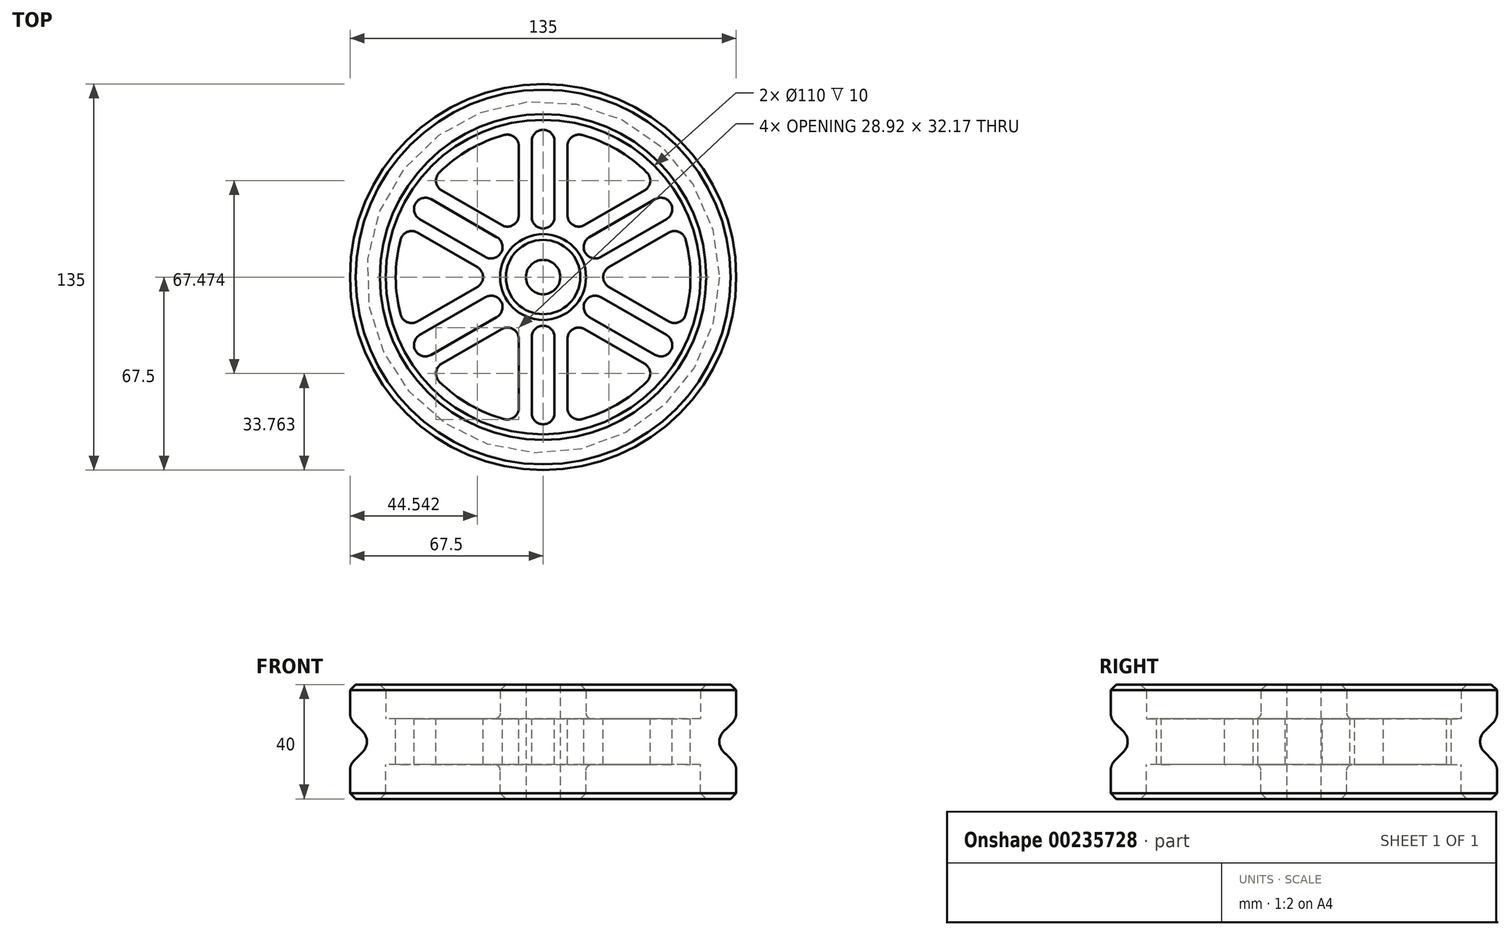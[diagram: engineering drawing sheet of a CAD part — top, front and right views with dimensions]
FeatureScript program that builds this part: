
annotation { "Feature Type Name" : "Feature", "Feature Type Description" : "" }
export const myFeature = defineFeature(function(context is Context, id is Id, definition is map)
    precondition{}
    {
        {
            var Q0;
            Q0=qCreatedBy(makeId("Top.planeOp"),FACE);
            var sketch = newSketch(context, id + "F0", { "sketchPlane" : qUnion([Q0])});
            skCircle(sketch, "E0", {"center": v(0, 0) * mm, "radius": 67.5 * mm});
            skCircle(sketch, "E1", {"center": v(0, 0) * mm, "radius": 55 * mm});
            skCircle(sketch, "E2", {"center": v(0, 0) * mm, "radius": 51.5 * mm});
            skCircle(sketch, "E3", {"center": v(0, 0) * mm, "radius": 47.5 * mm, "construction": true});
            skCircle(sketch, "E4", {"center": v(0, 0) * mm, "radius": 21 * mm, "construction": true});
            skCircle(sketch, "E5", {"center": v(0, 0) * mm, "radius": 6 * mm});
            skCircle(sketch, "E6", {"center": v(0, 0) * mm, "radius": 15 * mm});
            skCircle(sketch, "E7", {"center": v(0, 0) * mm, "radius": 17 * mm, "construction": true});
            skLineSegment(sketch, "E8", {"start": v(0, 0) * mm, "end": v(0, 51.5) * mm, "construction": true});
            skCircle(sketch, "E9", {"center": v(0, 21) * mm, "radius": 4 * mm});
            skCircle(sketch, "E10", {"center": v(0, 47.5) * mm, "radius": 4 * mm});
            skLineSegment(sketch, "E11", {"start": v(0, 0) * mm, "end": v(-41.14, 23.75) * mm, "construction": true});
            skLineSegment(sketch, "E12", {"start": v(0, 0) * mm, "end": v(-41.14, -23.75) * mm, "construction": true});
            skLineSegment(sketch, "E13", {"start": v(0, 0) * mm, "end": v(0, -47.5) * mm, "construction": true});
            skLineSegment(sketch, "E14", {"start": v(0, 0) * mm, "end": v(41.14, -23.75) * mm, "construction": true});
            skCircle(sketch, "E15", {"center": v(-18.19, 10.5) * mm, "radius": 4 * mm});
            skCircle(sketch, "E16", {"center": v(-41.14, 23.75) * mm, "radius": 4 * mm});
            skCircle(sketch, "E17", {"center": v(18.19, -10.5) * mm, "radius": 4 * mm});
            skCircle(sketch, "E18", {"center": v(0, -21) * mm, "radius": 4 * mm});
            skCircle(sketch, "E19", {"center": v(-18.19, -10.5) * mm, "radius": 4 * mm});
            skCircle(sketch, "E20", {"center": v(-41.14, -23.75) * mm, "radius": 4 * mm});
            skCircle(sketch, "E21", {"center": v(0, -47.5) * mm, "radius": 4 * mm});
            skCircle(sketch, "E22", {"center": v(41.14, -23.75) * mm, "radius": 4 * mm});
            skLineSegment(sketch, "E23", {"start": v(-39.14, 27.21) * mm, "end": v(-16.19, 13.96) * mm});
            skLineSegment(sketch, "E24", {"start": v(-16.19, 13.96) * mm, "end": v(-20.19, 7.04) * mm});
            skLineSegment(sketch, "E25", {"start": v(-20.19, 7.04) * mm, "end": v(-43.14, 20.29) * mm});
            skLineSegment(sketch, "E26", {"start": v(-4, 47.5) * mm, "end": v(-4, 21) * mm});
            skLineSegment(sketch, "E27", {"start": v(4, 47.5) * mm, "end": v(4, 21) * mm});
            skLineSegment(sketch, "E28", {"start": v(20.19, -7.04) * mm, "end": v(43.14, -20.29) * mm});
            skLineSegment(sketch, "E29", {"start": v(16.19, -13.96) * mm, "end": v(39.14, -27.21) * mm});
            skLineSegment(sketch, "E30", {"start": v(-16.19, -13.96) * mm, "end": v(-39.14, -27.21) * mm});
            skLineSegment(sketch, "E31", {"start": v(-43.14, -20.29) * mm, "end": v(-20.19, -7.04) * mm});
            skLineSegment(sketch, "E32", {"start": v(-4, -21) * mm, "end": v(-4, -47.5) * mm});
            skLineSegment(sketch, "E33", {"start": v(4, -21) * mm, "end": v(4, -47.5) * mm});
            skLineSegment(sketch, "E34.bottom", {"start": v(-8.5, 50.8) * mm, "end": v(8.5, 50.8) * mm, "construction": true});
            skLineSegment(sketch, "E34.top", {"start": v(-8.5, -50.8) * mm, "end": v(8.5, -50.8) * mm, "construction": true});
            skLineSegment(sketch, "E35", {"start": v(0, 0) * mm, "end": v(41.14, 23.75) * mm, "construction": true});
            skCircle(sketch, "E36", {"center": v(18.19, 10.5) * mm, "radius": 4 * mm});
            skCircle(sketch, "E37", {"center": v(41.14, 23.75) * mm, "radius": 4 * mm});
            skLineSegment(sketch, "E38", {"start": v(16.19, 13.96) * mm, "end": v(39.14, 27.21) * mm});
            skLineSegment(sketch, "E39", {"start": v(43.14, 20.29) * mm, "end": v(20.19, 7.04) * mm});
            skPoint(sketch, "E40.orphan", {"position": v(-39.74, -32.76) * mm});
            skPoint(sketch, "E41.orphan", {"position": v(39.74, -32.76) * mm});
            skPoint(sketch, "E42.orphan", {"position": v(48.24, 18.04) * mm});
            skPoint(sketch, "E43.orphan", {"position": v(39.74, 32.76) * mm});
            skLineSegment(sketch, "E44", {"start": v(-8.5, 14.72) * mm, "end": v(-39.74, 32.76) * mm});
            skLineSegment(sketch, "E45", {"start": v(-17, 0) * mm, "end": v(-48.24, 18.04) * mm});
            skLineSegment(sketch, "E46", {"start": v(-17, 0) * mm, "end": v(-48.24, -18.04) * mm});
            skLineSegment(sketch, "E47", {"start": v(-8.5, -14.72) * mm, "end": v(-39.74, -32.76) * mm});
            skLineSegment(sketch, "E48", {"start": v(8.5, -14.72) * mm, "end": v(39.74, -32.76) * mm});
            skLineSegment(sketch, "E49", {"start": v(17, 0) * mm, "end": v(48.24, -18.04) * mm});
            skLineSegment(sketch, "E50", {"start": v(17, 0) * mm, "end": v(48.24, 18.04) * mm});
            skLineSegment(sketch, "E51", {"start": v(8.5, 14.72) * mm, "end": v(39.74, 32.76) * mm});
            skLineSegment(sketch, "E52", {"start": v(-8.5, 50.8) * mm, "end": v(-8.5, 14.72) * mm});
            skLineSegment(sketch, "E53", {"start": v(8.5, 50.8) * mm, "end": v(8.5, 14.72) * mm});
            skLineSegment(sketch, "E54.trimOffspring", {"start": v(8.5, -14.72) * mm, "end": v(8.5, -50.8) * mm});
            skLineSegment(sketch, "E55.trimOffspring", {"start": v(-8.5, -14.72) * mm, "end": v(-8.5, -50.8) * mm});
            skLineSegment(sketch, "E56", {"start": v(-8.5, 14.72) * mm, "end": v(17, 0) * mm, "construction": true});
            skLineSegment(sketch, "E57", {"start": v(8.5, -14.72) * mm, "end": v(-17, 0) * mm, "construction": true});
            skLineSegment(sketch, "E58", {"start": v(-8.5, 14.72) * mm, "end": v(-8.5, -14.72) * mm, "construction": true});
            skLineSegment(sketch, "E59", {"start": v(-8.5, -14.72) * mm, "end": v(17, 0) * mm, "construction": true});
            skLineSegment(sketch, "E60", {"start": v(8.5, 14.72) * mm, "end": v(-17, 0) * mm, "construction": true});
            skLineSegment(sketch, "E61", {"start": v(8.5, -14.72) * mm, "end": v(8.5, 14.72) * mm, "construction": true});
            skSolve(sketch);
        }
        {
            var Q0;
            Q0=makeQuery(id+"F0.imprint","IMPRINT",FACE,{"disambiguationData":[TD([[makeQuery(id+"F0.imprint","IMPRINT",EDGE,{"derivedFrom":sQuery(id+"F0.wireOp",EDGE,"E0")}),1.0]])]});
            extrude(context, id + "F1", {"entities" : qUnion([Q0]), "depth" : 12 * mm});
        }
        {
            var Q0;
            Q0=makeQuery(id+"F0.imprint","IMPRINT",FACE,{"disambiguationData":[TD([[makeQuery(id+"F0.imprint","IMPRINT",EDGE,{"derivedFrom":sQuery(id+"F0.wireOp",EDGE,"E1")}),1.0]])]});
            var Q1;
            Q1=makeQuery(id+"F0.imprint","IMPRINT",FACE,{"disambiguationData":[TD([[makeQuery(id+"F0.imprint","IMPRINT",EDGE,{"derivedFrom":sQuery(id+"F0.wireOp",EDGE,"E6")}),-1.0]])]});
            extrude(context, id + "F2", {"entities" : qUnion([Q0, Q1]), "operationType" : NewBodyOperationType.ADD, "oppositeDirection" : true, "depth" : 8 * mm});
        }
        {
            var Q0;
            Q0=makeQuery(id+"F0.imprint","IMPRINT",FACE,{"disambiguationData":[TD([[makeQuery(id+"F0.imprint","IMPRINT",EDGE,{"derivedFrom":sQuery(id+"F0.wireOp",EDGE,"E5")}),-1.0]])]});
            extrude(context, id + "F3", {"entities" : qUnion([Q0]), "depth" : 12 * mm});
        }
        {
            var Q0;
            Q0=makeQuery(id+"F0.imprint","IMPRINT",FACE,{"disambiguationData":[TD([[makeQuery(id+"F0.imprint","IMPRINT",EDGE,{"derivedFrom":sQuery(id+"F0.wireOp",EDGE,"E5")}),-1.0]])]});
            extrude(context, id + "F4", {"entities" : qUnion([Q0]), "oppositeDirection" : true, "depth" : 8 * mm});
        }
        {
            var Q0;
            Q0=makeQuery(id+"F1.opExtrude","SWEPT_BODY",BODY,{"disambiguationData":[OSD([sQuery(id+"F0.wireOp",EDGE,"E0"),sQuery(id+"F0.wireOp",EDGE,"E1")])]});
            var Q1;
            Q1=makeQuery(id+"F2.opExtrude","SWEPT_BODY",BODY,{"disambiguationData":[OSD([sQuery(id+"F0.wireOp",EDGE,"E1"),sQuery(id+"F0.wireOp",EDGE,"E2"),sQuery(id+"F0.wireOp",EDGE,"E6"),sQuery(id+"F0.wireOp",EDGE,"E9"),sQuery(id+"F0.wireOp",EDGE,"E10"),sQuery(id+"F0.wireOp",EDGE,"E15"),sQuery(id+"F0.wireOp",EDGE,"E16"),sQuery(id+"F0.wireOp",EDGE,"E17"),sQuery(id+"F0.wireOp",EDGE,"E18"),sQuery(id+"F0.wireOp",EDGE,"E19"),sQuery(id+"F0.wireOp",EDGE,"E20"),sQuery(id+"F0.wireOp",EDGE,"E21"),sQuery(id+"F0.wireOp",EDGE,"E22"),sQuery(id+"F0.wireOp",EDGE,"E36"),sQuery(id+"F0.wireOp",EDGE,"E37"),sQuery(id+"F0.wireOp",EDGE,"E44"),sQuery(id+"F0.wireOp",EDGE,"E45"),sQuery(id+"F0.wireOp",EDGE,"E46"),sQuery(id+"F0.wireOp",EDGE,"E47"),sQuery(id+"F0.wireOp",EDGE,"E48"),sQuery(id+"F0.wireOp",EDGE,"E49"),sQuery(id+"F0.wireOp",EDGE,"E50"),sQuery(id+"F0.wireOp",EDGE,"E51"),sQuery(id+"F0.wireOp",EDGE,"E52"),sQuery(id+"F0.wireOp",EDGE,"E53"),sQuery(id+"F0.wireOp",EDGE,"E54.trimOffspring"),sQuery(id+"F0.wireOp",EDGE,"E55.trimOffspring")])]});
            var Q2;
            Q2=makeQuery(id+"F3.opExtrude","SWEPT_BODY",BODY,{"disambiguationData":[OSD([sQuery(id+"F0.wireOp",EDGE,"E5"),sQuery(id+"F0.wireOp",EDGE,"E6")])]});
            var Q3;
            Q3=makeQuery(id+"F4.opExtrude","SWEPT_BODY",BODY,{"disambiguationData":[OSD([sQuery(id+"F0.wireOp",EDGE,"E5"),sQuery(id+"F0.wireOp",EDGE,"E6")])]});
            booleanBodies(context, id + "F5", {"operationType" : BooleanOperationType.UNION, "tools" : qUnion([Q0, Q1, Q2, Q3])});
        }
        {
            var Q0;
            Q0=makeQuery(id+"F0.imprint","IMPRINT",FACE,{"disambiguationData":[TD([[makeQuery(id+"F0.imprint","IMPRINT",EDGE,{"derivedFrom":sQuery(id+"F0.wireOp",EDGE,"E0")}),1.0]])]});
            extrude(context, id + "F6", {"entities" : qUnion([Q0]), "oppositeDirection" : true, "depth" : 8 * mm});
        }
        {
            var Q0;
            Q0=makeQuery(id+"F6.opExtrude","SWEPT_BODY",BODY,{"disambiguationData":[OSD([sQuery(id+"F0.wireOp",EDGE,"E0"),sQuery(id+"F0.wireOp",EDGE,"E1")])]});
            var Q1;
            {var subQ0=sQuery(id+"F0.wireOp",EDGE,"E6");var subQ1=sQuery(id+"F0.wireOp",EDGE,"E5");var subQ2=sQuery(id+"F0.wireOp",EDGE,"E1");Q1=makeQuery(id+"F5.opBoolean","MERGE",BODY,{"derivedFrom":[makeQuery(id+"F1.opExtrude","SWEPT_BODY",BODY,{"disambiguationData":[OSD([sQuery(id+"F0.wireOp",EDGE,"E0"),subQ2])]}),makeQuery(id+"F2.opExtrude","SWEPT_BODY",BODY,{"disambiguationData":[OSD([subQ2,sQuery(id+"F0.wireOp",EDGE,"E2"),subQ0,sQuery(id+"F0.wireOp",EDGE,"E9"),sQuery(id+"F0.wireOp",EDGE,"E10"),sQuery(id+"F0.wireOp",EDGE,"E15"),sQuery(id+"F0.wireOp",EDGE,"E16"),sQuery(id+"F0.wireOp",EDGE,"E17"),sQuery(id+"F0.wireOp",EDGE,"E18"),sQuery(id+"F0.wireOp",EDGE,"E19"),sQuery(id+"F0.wireOp",EDGE,"E20"),sQuery(id+"F0.wireOp",EDGE,"E21"),sQuery(id+"F0.wireOp",EDGE,"E22"),sQuery(id+"F0.wireOp",EDGE,"E36"),sQuery(id+"F0.wireOp",EDGE,"E37"),sQuery(id+"F0.wireOp",EDGE,"E44"),sQuery(id+"F0.wireOp",EDGE,"E45"),sQuery(id+"F0.wireOp",EDGE,"E46"),sQuery(id+"F0.wireOp",EDGE,"E47"),sQuery(id+"F0.wireOp",EDGE,"E48"),sQuery(id+"F0.wireOp",EDGE,"E49"),sQuery(id+"F0.wireOp",EDGE,"E50"),sQuery(id+"F0.wireOp",EDGE,"E51"),sQuery(id+"F0.wireOp",EDGE,"E52"),sQuery(id+"F0.wireOp",EDGE,"E53"),sQuery(id+"F0.wireOp",EDGE,"E54.trimOffspring"),sQuery(id+"F0.wireOp",EDGE,"E55.trimOffspring")])]}),makeQuery(id+"F3.opExtrude","SWEPT_BODY",BODY,{"disambiguationData":[OSD([subQ1,subQ0])]}),makeQuery(id+"F4.opExtrude","SWEPT_BODY",BODY,{"disambiguationData":[OSD([subQ1,subQ0])]})]});}
            var Q2;
            Q2=makeQuery(id+"F1.opExtrude","SWEPT_BODY",BODY,{"disambiguationData":[OSD([sQuery(id+"F0.wireOp",EDGE,"E0"),sQuery(id+"F0.wireOp",EDGE,"E1")])]});
            booleanBodies(context, id + "F7", {"operationType" : BooleanOperationType.UNION, "tools" : qUnion([Q0, Q1, Q2])});
        }
        {
            var Q0;
            Q0=makeQuery(id+"F6.opExtrude","CAP_EDGE",EDGE,{"disambiguationData":[OSD([sQuery(id+"F0.wireOp",EDGE,"E0")])],"isStart":false});
            chamfer(context, id + "F8", {"entities" : qUnion([Q0]), "chamferType" : ChamferType.TWO_OFFSETS, "width1" : 8 * mm, "oppositeDirection" : false, "width2" : 8 * mm, "tangentPropagation" : true});
        }
        {
            var Q0;
            Q0=makeQuery(id+"F6.opExtrude","SWEPT_BODY",BODY,{"disambiguationData":[OSD([sQuery(id+"F0.wireOp",EDGE,"E0"),sQuery(id+"F0.wireOp",EDGE,"E1")])]});
            var Q1;
            {var subQ0=sQuery(id+"F0.wireOp",EDGE,"E1");var subQ1=sQuery(id+"F0.wireOp",EDGE,"E6");Q1=makeQuery(id+"F7.opBoolean","MERGE",FACE,{"derivedFrom":[makeQuery(id+"F5.opBoolean","MERGE",FACE,{"derivedFrom":[makeQuery(id+"F2.opExtrude","CAP_FACE",FACE,{"disambiguationData":[OSD([subQ0,sQuery(id+"F0.wireOp",EDGE,"E2"),subQ1,sQuery(id+"F0.wireOp",EDGE,"E9"),sQuery(id+"F0.wireOp",EDGE,"E10"),sQuery(id+"F0.wireOp",EDGE,"E15"),sQuery(id+"F0.wireOp",EDGE,"E16"),sQuery(id+"F0.wireOp",EDGE,"E17"),sQuery(id+"F0.wireOp",EDGE,"E18"),sQuery(id+"F0.wireOp",EDGE,"E19"),sQuery(id+"F0.wireOp",EDGE,"E20"),sQuery(id+"F0.wireOp",EDGE,"E21"),sQuery(id+"F0.wireOp",EDGE,"E22"),sQuery(id+"F0.wireOp",EDGE,"E36"),sQuery(id+"F0.wireOp",EDGE,"E37"),sQuery(id+"F0.wireOp",EDGE,"E44"),sQuery(id+"F0.wireOp",EDGE,"E45"),sQuery(id+"F0.wireOp",EDGE,"E46"),sQuery(id+"F0.wireOp",EDGE,"E47"),sQuery(id+"F0.wireOp",EDGE,"E48"),sQuery(id+"F0.wireOp",EDGE,"E49"),sQuery(id+"F0.wireOp",EDGE,"E50"),sQuery(id+"F0.wireOp",EDGE,"E51"),sQuery(id+"F0.wireOp",EDGE,"E52"),sQuery(id+"F0.wireOp",EDGE,"E53"),sQuery(id+"F0.wireOp",EDGE,"E54.trimOffspring"),sQuery(id+"F0.wireOp",EDGE,"E55.trimOffspring")])],"isStart":false}),makeQuery(id+"F4.opExtrude","CAP_FACE",FACE,{"disambiguationData":[OSD([sQuery(id+"F0.wireOp",EDGE,"E5"),subQ1])],"isStart":false})]}),makeQuery(id+"F6.opExtrude","CAP_FACE",FACE,{"disambiguationData":[OSD([sQuery(id+"F0.wireOp",EDGE,"E0"),subQ0])],"isStart":false})]});}
            mirror(context, id + "F9", {"operationType" : NewBodyOperationType.ADD, "entities" : qUnion([Q0]), "mirrorPlane" : qUnion([Q1])});
        }
        {
            var Q0;
            {var subQ0=sQuery(id+"F0.wireOp",EDGE,"E1");var subQ1=sQuery(id+"F0.wireOp",EDGE,"E0");var subQ2=sQuery(id+"F0.wireOp",EDGE,"E6");var subQ3=makeQuery(id+"F8.opChamfer","BLEND_EDGE",EDGE,{"blendedFrom":[makeQuery(id+"F6.opExtrude","CAP_EDGE",EDGE,{"disambiguationData":[OSD([subQ1])],"isStart":false}),makeQuery(id+"F7.opBoolean","MERGE",FACE,{"derivedFrom":[makeQuery(id+"F5.opBoolean","MERGE",FACE,{"derivedFrom":[makeQuery(id+"F2.opExtrude","CAP_FACE",FACE,{"disambiguationData":[OSD([subQ0,sQuery(id+"F0.wireOp",EDGE,"E2"),subQ2,sQuery(id+"F0.wireOp",EDGE,"E9"),sQuery(id+"F0.wireOp",EDGE,"E10"),sQuery(id+"F0.wireOp",EDGE,"E15"),sQuery(id+"F0.wireOp",EDGE,"E16"),sQuery(id+"F0.wireOp",EDGE,"E17"),sQuery(id+"F0.wireOp",EDGE,"E18"),sQuery(id+"F0.wireOp",EDGE,"E19"),sQuery(id+"F0.wireOp",EDGE,"E20"),sQuery(id+"F0.wireOp",EDGE,"E21"),sQuery(id+"F0.wireOp",EDGE,"E22"),sQuery(id+"F0.wireOp",EDGE,"E36"),sQuery(id+"F0.wireOp",EDGE,"E37"),sQuery(id+"F0.wireOp",EDGE,"E44"),sQuery(id+"F0.wireOp",EDGE,"E45"),sQuery(id+"F0.wireOp",EDGE,"E46"),sQuery(id+"F0.wireOp",EDGE,"E47"),sQuery(id+"F0.wireOp",EDGE,"E48"),sQuery(id+"F0.wireOp",EDGE,"E49"),sQuery(id+"F0.wireOp",EDGE,"E50"),sQuery(id+"F0.wireOp",EDGE,"E51"),sQuery(id+"F0.wireOp",EDGE,"E52"),sQuery(id+"F0.wireOp",EDGE,"E53"),sQuery(id+"F0.wireOp",EDGE,"E54.trimOffspring"),sQuery(id+"F0.wireOp",EDGE,"E55.trimOffspring")])],"isStart":false}),makeQuery(id+"F4.opExtrude","CAP_FACE",FACE,{"disambiguationData":[OSD([sQuery(id+"F0.wireOp",EDGE,"E5"),subQ2])],"isStart":false})]}),makeQuery(id+"F6.opExtrude","CAP_FACE",FACE,{"disambiguationData":[OSD([subQ1,subQ0])],"isStart":false})]})],"blendedInto":[makeQuery(id+"F7.opBoolean","MERGE",FACE,{"derivedFrom":[makeQuery(id+"F5.opBoolean","MERGE",FACE,{"derivedFrom":[makeQuery(id+"F2.opExtrude","CAP_FACE",FACE,{"disambiguationData":[OSD([subQ0,sQuery(id+"F0.wireOp",EDGE,"E2"),subQ2,sQuery(id+"F0.wireOp",EDGE,"E9"),sQuery(id+"F0.wireOp",EDGE,"E10"),sQuery(id+"F0.wireOp",EDGE,"E15"),sQuery(id+"F0.wireOp",EDGE,"E16"),sQuery(id+"F0.wireOp",EDGE,"E17"),sQuery(id+"F0.wireOp",EDGE,"E18"),sQuery(id+"F0.wireOp",EDGE,"E19"),sQuery(id+"F0.wireOp",EDGE,"E20"),sQuery(id+"F0.wireOp",EDGE,"E21"),sQuery(id+"F0.wireOp",EDGE,"E22"),sQuery(id+"F0.wireOp",EDGE,"E36"),sQuery(id+"F0.wireOp",EDGE,"E37"),sQuery(id+"F0.wireOp",EDGE,"E44"),sQuery(id+"F0.wireOp",EDGE,"E45"),sQuery(id+"F0.wireOp",EDGE,"E46"),sQuery(id+"F0.wireOp",EDGE,"E47"),sQuery(id+"F0.wireOp",EDGE,"E48"),sQuery(id+"F0.wireOp",EDGE,"E49"),sQuery(id+"F0.wireOp",EDGE,"E50"),sQuery(id+"F0.wireOp",EDGE,"E51"),sQuery(id+"F0.wireOp",EDGE,"E52"),sQuery(id+"F0.wireOp",EDGE,"E53"),sQuery(id+"F0.wireOp",EDGE,"E54.trimOffspring"),sQuery(id+"F0.wireOp",EDGE,"E55.trimOffspring")])],"isStart":false}),makeQuery(id+"F4.opExtrude","CAP_FACE",FACE,{"disambiguationData":[OSD([sQuery(id+"F0.wireOp",EDGE,"E5"),subQ2])],"isStart":false})]}),makeQuery(id+"F6.opExtrude","CAP_FACE",FACE,{"disambiguationData":[OSD([subQ1,subQ0])],"isStart":false})]})]});Q0=makeQuery(id+"F9.boolean.opBoolean","MERGE",EDGE,{"derivedFrom":[subQ3,makeQuery(id+"F9.opPattern","COPY",EDGE,{"derivedFrom":subQ3,"instanceName":"1"})]});}
            var Q1;
            {var subQ0=sQuery(id+"F0.wireOp",EDGE,"E0");Q1=makeQuery(id+"F9.opPattern","COPY",EDGE,{"derivedFrom":makeQuery(id+"F8.opChamfer","BLEND_EDGE",EDGE,{"blendedFrom":[makeQuery(id+"F6.opExtrude","CAP_EDGE",EDGE,{"disambiguationData":[OSD([subQ0])],"isStart":false}),makeQuery(id+"F7.opBoolean","MERGE",FACE,{"derivedFrom":[makeQuery(id+"F1.opExtrude","SWEPT_FACE",FACE,{"disambiguationData":[OSD([subQ0])]}),makeQuery(id+"F6.opExtrude","SWEPT_FACE",FACE,{"disambiguationData":[OSD([subQ0])]})]})],"blendedInto":[makeQuery(id+"F7.opBoolean","MERGE",FACE,{"derivedFrom":[makeQuery(id+"F1.opExtrude","SWEPT_FACE",FACE,{"disambiguationData":[OSD([subQ0])]}),makeQuery(id+"F6.opExtrude","SWEPT_FACE",FACE,{"disambiguationData":[OSD([subQ0])]})]})]}),"instanceName":"1"});}
            var Q2;
            {var subQ0=sQuery(id+"F0.wireOp",EDGE,"E0");Q2=makeQuery(id+"F8.opChamfer","BLEND_EDGE",EDGE,{"blendedFrom":[makeQuery(id+"F6.opExtrude","CAP_EDGE",EDGE,{"disambiguationData":[OSD([subQ0])],"isStart":false}),makeQuery(id+"F7.opBoolean","MERGE",FACE,{"derivedFrom":[makeQuery(id+"F1.opExtrude","SWEPT_FACE",FACE,{"disambiguationData":[OSD([subQ0])]}),makeQuery(id+"F6.opExtrude","SWEPT_FACE",FACE,{"disambiguationData":[OSD([subQ0])]})]})],"blendedInto":[makeQuery(id+"F7.opBoolean","MERGE",FACE,{"derivedFrom":[makeQuery(id+"F1.opExtrude","SWEPT_FACE",FACE,{"disambiguationData":[OSD([subQ0])]}),makeQuery(id+"F6.opExtrude","SWEPT_FACE",FACE,{"disambiguationData":[OSD([subQ0])]})]})]});}
            fillet(context, id + "F10", {"entities" : qUnion([Q0, Q1, Q2]), "radius" : 5 * mm, "tangentPropagation" : true, "allowEdgeOverflow" : false});
        }
        {
            var Q0;
            Q0=makeQuery(id+"F1.opExtrude","CAP_EDGE",EDGE,{"disambiguationData":[OSD([sQuery(id+"F0.wireOp",EDGE,"E0")])],"isStart":false});
            var Q1;
            Q1=makeQuery(id+"F9.opPattern","COPY",EDGE,{"derivedFrom":makeQuery(id+"F1.opExtrude","CAP_EDGE",EDGE,{"disambiguationData":[OSD([sQuery(id+"F0.wireOp",EDGE,"E0")])],"isStart":false}),"instanceName":"1"});
            var Q2;
            Q2=makeQuery(id+"F9.opPattern","COPY",EDGE,{"derivedFrom":makeQuery(id+"F1.opExtrude","CAP_EDGE",EDGE,{"disambiguationData":[OSD([sQuery(id+"F0.wireOp",EDGE,"E1")])],"isStart":false}),"instanceName":"1"});
            var Q3;
            Q3=makeQuery(id+"F9.opPattern","COPY",EDGE,{"derivedFrom":makeQuery(id+"F3.opExtrude","CAP_EDGE",EDGE,{"disambiguationData":[OSD([sQuery(id+"F0.wireOp",EDGE,"E6")])],"isStart":false}),"instanceName":"1"});
            var Q4;
            Q4=makeQuery(id+"F1.opExtrude","CAP_EDGE",EDGE,{"disambiguationData":[OSD([sQuery(id+"F0.wireOp",EDGE,"E1")])],"isStart":false});
            var Q5;
            Q5=makeQuery(id+"F3.opExtrude","CAP_EDGE",EDGE,{"disambiguationData":[OSD([sQuery(id+"F0.wireOp",EDGE,"E6")])],"isStart":false});
            chamfer(context, id + "F11", {"entities" : qUnion([Q0, Q1, Q2, Q3, Q4, Q5]), "width" : 2 * mm, "tangentPropagation" : true});
        }
        {
            var Q0;
            {var subQ0=makeQuery(id+"F2.opExtrude","SWEPT_EDGE",EDGE,{"disambiguationData":[OSD([sQuery(id+"F0.wireOp",EDGE,"E2"),sQuery(id+"F0.wireOp",EDGE,"E44")])]});Q0=makeQuery(id+"F9.boolean.opBoolean","MERGE",EDGE,{"derivedFrom":[subQ0,makeQuery(id+"F9.opPattern","COPY",EDGE,{"derivedFrom":subQ0,"instanceName":"1"})]});}
            var Q1;
            {var subQ0=makeQuery(id+"F2.opExtrude","SWEPT_EDGE",EDGE,{"disambiguationData":[OSD([sQuery(id+"F0.wireOp",EDGE,"E2"),sQuery(id+"F0.wireOp",EDGE,"E45")])]});Q1=makeQuery(id+"F9.boolean.opBoolean","MERGE",EDGE,{"derivedFrom":[subQ0,makeQuery(id+"F9.opPattern","COPY",EDGE,{"derivedFrom":subQ0,"instanceName":"1"})]});}
            var Q2;
            {var subQ0=makeQuery(id+"F2.opExtrude","SWEPT_EDGE",EDGE,{"disambiguationData":[OSD([sQuery(id+"F0.wireOp",EDGE,"E2"),sQuery(id+"F0.wireOp",EDGE,"E53")])]});Q2=makeQuery(id+"F9.boolean.opBoolean","MERGE",EDGE,{"derivedFrom":[subQ0,makeQuery(id+"F9.opPattern","COPY",EDGE,{"derivedFrom":subQ0,"instanceName":"1"})]});}
            var Q3;
            {var subQ0=makeQuery(id+"F2.opExtrude","SWEPT_EDGE",EDGE,{"disambiguationData":[OSD([sQuery(id+"F0.wireOp",EDGE,"E2"),sQuery(id+"F0.wireOp",EDGE,"E50")])]});Q3=makeQuery(id+"F9.boolean.opBoolean","MERGE",EDGE,{"derivedFrom":[subQ0,makeQuery(id+"F9.opPattern","COPY",EDGE,{"derivedFrom":subQ0,"instanceName":"1"})]});}
            var Q4;
            {var subQ0=makeQuery(id+"F2.opExtrude","SWEPT_EDGE",EDGE,{"disambiguationData":[OSD([sQuery(id+"F0.wireOp",EDGE,"E2"),sQuery(id+"F0.wireOp",EDGE,"E51")])]});Q4=makeQuery(id+"F9.boolean.opBoolean","MERGE",EDGE,{"derivedFrom":[subQ0,makeQuery(id+"F9.opPattern","COPY",EDGE,{"derivedFrom":subQ0,"instanceName":"1"})]});}
            var Q5;
            {var subQ0=makeQuery(id+"F2.opExtrude","SWEPT_EDGE",EDGE,{"disambiguationData":[OSD([sQuery(id+"F0.wireOp",EDGE,"E2"),sQuery(id+"F0.wireOp",EDGE,"E48")])]});Q5=makeQuery(id+"F9.boolean.opBoolean","MERGE",EDGE,{"derivedFrom":[subQ0,makeQuery(id+"F9.opPattern","COPY",EDGE,{"derivedFrom":subQ0,"instanceName":"1"})]});}
            var Q6;
            {var subQ0=makeQuery(id+"F2.opExtrude","SWEPT_EDGE",EDGE,{"disambiguationData":[OSD([sQuery(id+"F0.wireOp",EDGE,"E2"),sQuery(id+"F0.wireOp",EDGE,"E49")])]});Q6=makeQuery(id+"F9.boolean.opBoolean","MERGE",EDGE,{"derivedFrom":[subQ0,makeQuery(id+"F9.opPattern","COPY",EDGE,{"derivedFrom":subQ0,"instanceName":"1"})]});}
            var Q7;
            {var subQ0=makeQuery(id+"F2.opExtrude","SWEPT_EDGE",EDGE,{"disambiguationData":[OSD([sQuery(id+"F0.wireOp",EDGE,"E2"),sQuery(id+"F0.wireOp",EDGE,"E55.trimOffspring")])]});Q7=makeQuery(id+"F9.boolean.opBoolean","MERGE",EDGE,{"derivedFrom":[subQ0,makeQuery(id+"F9.opPattern","COPY",EDGE,{"derivedFrom":subQ0,"instanceName":"1"})]});}
            var Q8;
            {var subQ0=makeQuery(id+"F2.opExtrude","SWEPT_EDGE",EDGE,{"disambiguationData":[OSD([sQuery(id+"F0.wireOp",EDGE,"E2"),sQuery(id+"F0.wireOp",EDGE,"E54.trimOffspring")])]});Q8=makeQuery(id+"F9.boolean.opBoolean","MERGE",EDGE,{"derivedFrom":[subQ0,makeQuery(id+"F9.opPattern","COPY",EDGE,{"derivedFrom":subQ0,"instanceName":"1"})]});}
            var Q9;
            {var subQ0=makeQuery(id+"F2.opExtrude","SWEPT_EDGE",EDGE,{"disambiguationData":[OSD([sQuery(id+"F0.wireOp",EDGE,"E2"),sQuery(id+"F0.wireOp",EDGE,"E46")])]});Q9=makeQuery(id+"F9.boolean.opBoolean","MERGE",EDGE,{"derivedFrom":[subQ0,makeQuery(id+"F9.opPattern","COPY",EDGE,{"derivedFrom":subQ0,"instanceName":"1"})]});}
            var Q10;
            {var subQ0=makeQuery(id+"F2.opExtrude","SWEPT_EDGE",EDGE,{"disambiguationData":[OSD([sQuery(id+"F0.wireOp",EDGE,"E2"),sQuery(id+"F0.wireOp",EDGE,"E47")])]});Q10=makeQuery(id+"F9.boolean.opBoolean","MERGE",EDGE,{"derivedFrom":[subQ0,makeQuery(id+"F9.opPattern","COPY",EDGE,{"derivedFrom":subQ0,"instanceName":"1"})]});}
            var Q11;
            {var subQ0=makeQuery(id+"F2.opExtrude","SWEPT_EDGE",EDGE,{"disambiguationData":[OSD([sQuery(id+"F0.wireOp",EDGE,"E2"),sQuery(id+"F0.wireOp",EDGE,"E52")])]});Q11=makeQuery(id+"F9.boolean.opBoolean","MERGE",EDGE,{"derivedFrom":[subQ0,makeQuery(id+"F9.opPattern","COPY",EDGE,{"derivedFrom":subQ0,"instanceName":"1"})]});}
            fillet(context, id + "F12", {"entities" : qUnion([Q0, Q1, Q2, Q3, Q4, Q5, Q6, Q7, Q8, Q9, Q10, Q11]), "radius" : 4 * mm, "tangentPropagation" : true, "allowEdgeOverflow" : false});
        }
        {
            var Q0;
            {var subQ0=makeQuery(id+"F2.opExtrude","SWEPT_EDGE",EDGE,{"disambiguationData":[OSD([sQuery(id+"F0.wireOp",EDGE,"E48"),sQuery(id+"F0.wireOp",EDGE,"E54.trimOffspring")])]});Q0=makeQuery(id+"F9.boolean.opBoolean","MERGE",EDGE,{"derivedFrom":[subQ0,makeQuery(id+"F9.opPattern","COPY",EDGE,{"derivedFrom":subQ0,"instanceName":"1"})]});}
            var Q1;
            {var subQ0=makeQuery(id+"F2.opExtrude","SWEPT_EDGE",EDGE,{"disambiguationData":[OSD([sQuery(id+"F0.wireOp",EDGE,"E49"),sQuery(id+"F0.wireOp",EDGE,"E50")])]});Q1=makeQuery(id+"F9.boolean.opBoolean","MERGE",EDGE,{"derivedFrom":[subQ0,makeQuery(id+"F9.opPattern","COPY",EDGE,{"derivedFrom":subQ0,"instanceName":"1"})]});}
            var Q2;
            {var subQ0=makeQuery(id+"F2.opExtrude","SWEPT_EDGE",EDGE,{"disambiguationData":[OSD([sQuery(id+"F0.wireOp",EDGE,"E51"),sQuery(id+"F0.wireOp",EDGE,"E53")])]});Q2=makeQuery(id+"F9.boolean.opBoolean","MERGE",EDGE,{"derivedFrom":[subQ0,makeQuery(id+"F9.opPattern","COPY",EDGE,{"derivedFrom":subQ0,"instanceName":"1"})]});}
            var Q3;
            {var subQ0=makeQuery(id+"F2.opExtrude","SWEPT_EDGE",EDGE,{"disambiguationData":[OSD([sQuery(id+"F0.wireOp",EDGE,"E44"),sQuery(id+"F0.wireOp",EDGE,"E52")])]});Q3=makeQuery(id+"F9.boolean.opBoolean","MERGE",EDGE,{"derivedFrom":[subQ0,makeQuery(id+"F9.opPattern","COPY",EDGE,{"derivedFrom":subQ0,"instanceName":"1"})]});}
            var Q4;
            {var subQ0=makeQuery(id+"F2.opExtrude","SWEPT_EDGE",EDGE,{"disambiguationData":[OSD([sQuery(id+"F0.wireOp",EDGE,"E45"),sQuery(id+"F0.wireOp",EDGE,"E46")])]});Q4=makeQuery(id+"F9.boolean.opBoolean","MERGE",EDGE,{"derivedFrom":[subQ0,makeQuery(id+"F9.opPattern","COPY",EDGE,{"derivedFrom":subQ0,"instanceName":"1"})]});}
            var Q5;
            {var subQ0=makeQuery(id+"F2.opExtrude","SWEPT_EDGE",EDGE,{"disambiguationData":[OSD([sQuery(id+"F0.wireOp",EDGE,"E47"),sQuery(id+"F0.wireOp",EDGE,"E55.trimOffspring")])]});Q5=makeQuery(id+"F9.boolean.opBoolean","MERGE",EDGE,{"derivedFrom":[subQ0,makeQuery(id+"F9.opPattern","COPY",EDGE,{"derivedFrom":subQ0,"instanceName":"1"})]});}
            fillet(context, id + "F13", {"entities" : qUnion([Q0, Q1, Q2, Q3, Q4, Q5]), "radius" : 4 * mm, "tangentPropagation" : true, "allowEdgeOverflow" : false});
        }
        {
            var Q0;
            Q0=makeQuery(id+"F2.opExtrude","CAP_EDGE",EDGE,{"disambiguationData":[OSD([sQuery(id+"F0.wireOp",EDGE,"E6")])],"isStart":true});
            var Q1;
            Q1=makeQuery(id+"F9.opPattern","COPY",EDGE,{"derivedFrom":makeQuery(id+"F2.opExtrude","CAP_EDGE",EDGE,{"disambiguationData":[OSD([sQuery(id+"F0.wireOp",EDGE,"E6")])],"isStart":true}),"instanceName":"1"});
            fillet(context, id + "F14", {"entities" : qUnion([Q0, Q1]), "radius" : 2 * mm, "tangentPropagation" : true, "allowEdgeOverflow" : false});
        }
    });
